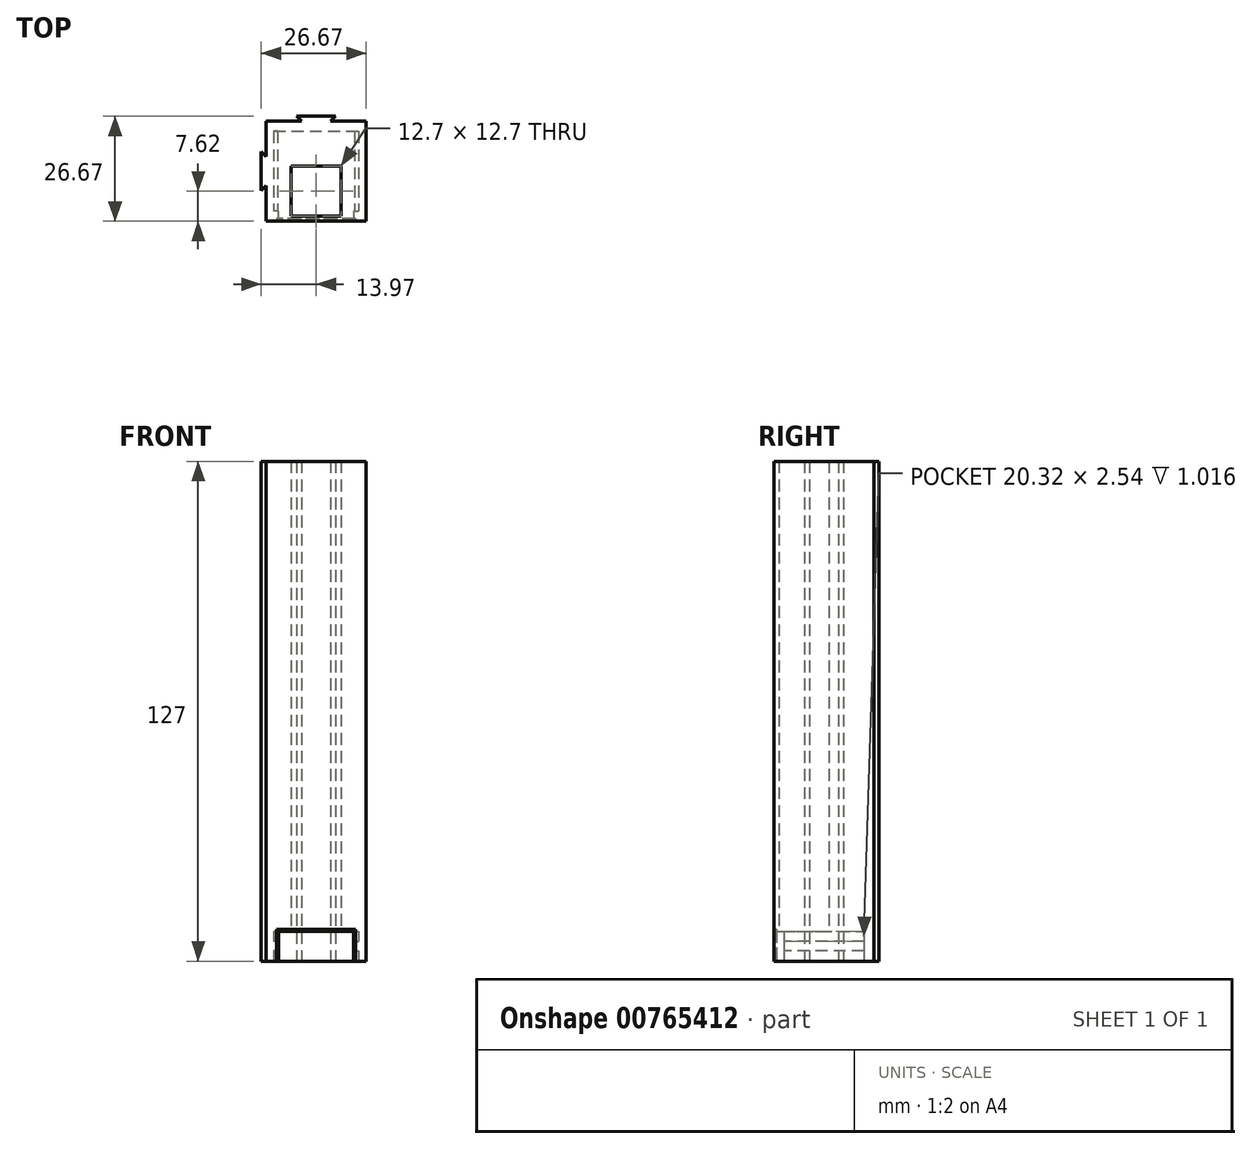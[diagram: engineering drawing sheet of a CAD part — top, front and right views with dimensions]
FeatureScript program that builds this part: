
annotation { "Feature Type Name" : "Feature", "Feature Type Description" : "" }
export const myFeature = defineFeature(function(context is Context, id is Id, definition is map)
    precondition{}
    {
        {
            var Q0;
            Q0=qCreatedBy(makeId("Top.planeOp"),FACE);
            var sketch = newSketch(context, id + "F0", { "sketchPlane" : qUnion([Q0])});
            skLineSegment(sketch, "E0.bottom", {"start": v(12.7, 12.7) * mm, "end": v(-12.7, 12.7) * mm});
            skLineSegment(sketch, "E0.top", {"start": v(12.7, -12.7) * mm, "end": v(-12.7, -12.7) * mm});
            skLineSegment(sketch, "E0.left", {"start": v(12.7, 12.7) * mm, "end": v(12.7, -12.7) * mm});
            skLineSegment(sketch, "E0.right", {"start": v(-12.7, 12.7) * mm, "end": v(-12.7, -12.7) * mm});
            skPoint(sketch, "E0.middle", {"position": v(0, 0) * mm});
            skLineSegment(sketch, "E1", {"start": v(-3.68, 12.7) * mm, "end": v(-4.95, 13.97) * mm});
            skLineSegment(sketch, "E2", {"start": v(-4.95, 13.97) * mm, "end": v(4.95, 13.97) * mm});
            skLineSegment(sketch, "E3", {"start": v(4.95, 13.97) * mm, "end": v(3.68, 12.7) * mm});
            skLineSegment(sketch, "E4.MirrorCS", {"start": v(-12.7, 3.68) * mm, "end": v(-13.97, 4.95) * mm});
            skLineSegment(sketch, "E5.MirrorCS", {"start": v(-13.97, 4.95) * mm, "end": v(-13.97, -4.95) * mm});
            skLineSegment(sketch, "E6.MirrorCS", {"start": v(-13.97, -4.95) * mm, "end": v(-12.7, -3.68) * mm});
            skLineSegment(sketch, "E7.bottom", {"start": v(-6.35, -11.43) * mm, "end": v(6.35, -11.43) * mm});
            skLineSegment(sketch, "E7.top", {"start": v(-6.35, 1.27) * mm, "end": v(6.35, 1.27) * mm});
            skLineSegment(sketch, "E7.left", {"start": v(-6.35, -11.43) * mm, "end": v(-6.35, 1.27) * mm});
            skLineSegment(sketch, "E7.right", {"start": v(6.35, -11.43) * mm, "end": v(6.35, 1.27) * mm});
            skPoint(sketch, "E7.middle", {"position": v(0, -5.08) * mm});
            skSolve(sketch);
        }
        {
            var Q0;
            Q0=makeQuery(id+"F0.imprint","IMPRINT",FACE,{"disambiguationData":[TD([[makeQuery(id+"F0.imprint","IMPRINT",EDGE,{"derivedFrom":sQuery(id+"F0.wireOp",EDGE,"Ek69CNRn-8RVK-RxQl-53fH-Jz5PkY7OIrkr")}),-1.0]])]});
            var Q1;
            {var subQ0=sQuery(id+"F0.wireOp",EDGE,"E4.MirrorCS");Q1=makeQuery(id+"F0.imprint","IMPRINT",FACE,{"disambiguationData":[TD([[makeQuery(id+"F0.imprint","IMPRINT",EDGE,{"derivedFrom":subQ0}),1.0]])]});}
            var Q2;
            {var subQ0=sQuery(id+"F0.wireOp",EDGE,"648ae852-5b30-4ce4-b5d7-663e1538fe900.MirrorCS");Q2=makeQuery(id+"F0.imprint","IMPRINT",FACE,{"disambiguationData":[TD([[makeQuery(id+"F0.imprint","IMPRINT",EDGE,{"derivedFrom":subQ0}),1.0]])]});}
            var Q3;
            {var subQ0=sQuery(id+"F0.wireOp",EDGE,"995b501b-87b1-40df-89db-5718103b703a");Q3=makeQuery(id+"F0.imprint","IMPRINT",FACE,{"disambiguationData":[TD([[makeQuery(id+"F0.imprint","IMPRINT",EDGE,{"derivedFrom":subQ0}),-1.0]])]});}
            var Q4;
            {var subQ0=sQuery(id+"F0.wireOp",EDGE,"E1");Q4=makeQuery(id+"F0.imprint","IMPRINT",FACE,{"disambiguationData":[TD([[makeQuery(id+"F0.imprint","IMPRINT",EDGE,{"derivedFrom":subQ0}),-1.0]])]});}
            var Q5;
            {var subQ1=sQuery(id+"F0.wireOp",EDGE,"E0.top");Q5=makeQuery(id+"F0.imprint","IMPRINT",FACE,{"disambiguationData":[TD([[makeQuery(id+"F0.imprint","IMPRINT",EDGE,{"derivedFrom":subQ1}),-1.0]])]});}
            extrude(context, id + "F1", {"entities" : qUnion([Q0, Q1, Q2, Q3, Q4, Q5]), "depth" : 127 * mm, "offsetDistance" : 25.4 * mm});
        }
        {
            var Q0;
            Q0=makeQuery(id+"F1.opExtrude","CAP_FACE",FACE,{"disambiguationData":[OSD([sQuery(id+"F0.wireOp",EDGE,"E0.bottom"),sQuery(id+"F0.wireOp",EDGE,"E0.top"),sQuery(id+"F0.wireOp",EDGE,"E0.left"),sQuery(id+"F0.wireOp",EDGE,"E0.right"),sQuery(id+"F0.wireOp",EDGE,"E1"),sQuery(id+"F0.wireOp",EDGE,"E2"),sQuery(id+"F0.wireOp",EDGE,"E3"),sQuery(id+"F0.wireOp",EDGE,"995b501b-87b1-40df-89db-5718103b703a"),sQuery(id+"F0.wireOp",EDGE,"d9b632a0-34b0-463a-8696-1e9d1799fc8a"),sQuery(id+"F0.wireOp",EDGE,"b3bc504c-1797-48d5-8887-40c9249a8113"),sQuery(id+"F0.wireOp",EDGE,"E4.MirrorCS"),sQuery(id+"F0.wireOp",EDGE,"E5.MirrorCS"),sQuery(id+"F0.wireOp",EDGE,"E6.MirrorCS"),sQuery(id+"F0.wireOp",EDGE,"Ek69CNRn-8RVK-RxQl-53fH-Jz5PkY7OIrkr")])],"isStart":true});
            var sketch = newSketch(context, id + "F2", { "sketchPlane" : qUnion([Q0])});
            skLineSegment(sketch, "E8", {"start": v(-9.52, 12.7) * mm, "end": v(-9.52, 10.16) * mm});
            skLineSegment(sketch, "E9", {"start": v(-9.52, 10.16) * mm, "end": v(-10.8, 10.16) * mm});
            skLineSegment(sketch, "E10", {"start": v(-10.8, 10.16) * mm, "end": v(-10.8, -10.16) * mm});
            skLineSegment(sketch, "E11", {"start": v(-10.8, -10.16) * mm, "end": v(10.8, -10.16) * mm});
            skLineSegment(sketch, "E12", {"start": v(10.8, -10.16) * mm, "end": v(10.8, 10.16) * mm});
            skLineSegment(sketch, "E13", {"start": v(9.52, 10.16) * mm, "end": v(10.8, 10.16) * mm});
            skLineSegment(sketch, "E14", {"start": v(9.52, 10.16) * mm, "end": v(9.52, 12.7) * mm});
            skLineSegment(sketch, "E15", {"start": v(9.52, 12.7) * mm, "end": v(-9.52, 12.7) * mm});
            skSolve(sketch);
        }
        {
            var Q0;
            Q0=makeQuery(id+"F2.imprint","IMPRINT",FACE,{"disambiguationData":[TD([[makeQuery(id+"F2.imprint","IMPRINT",EDGE,{"derivedFrom":sQuery(id+"F2.wireOp",EDGE,"E8")}),1.0]])]});
            extrude(context, id + "F3", {"entities" : qUnion([Q0]), "operationType" : NewBodyOperationType.REMOVE, "oppositeDirection" : true, "depth" : 7.62 * mm, "offsetDistance" : 25.4 * mm});
        }
        {
            var Q0;
            Q0=makeQuery(id+"F1.opExtrude","SWEPT_FACE",FACE,{"disambiguationData":[OSD([sQuery(id+"F0.wireOp",EDGE,"E0.top")])]});
            var sketch = newSketch(context, id + "F4", { "sketchPlane" : qUnion([Q0])});
            skLineSegment(sketch, "E16.0", {"start": v(-10.03, 8.13) * mm, "end": v(-10.03, 0) * mm});
            skLineSegment(sketch, "E16.1", {"start": v(10.03, 8.13) * mm, "end": v(-10.03, 8.13) * mm});
            skLineSegment(sketch, "E16.2", {"start": v(10.03, 8.13) * mm, "end": v(10.03, 0) * mm});
            skSolve(sketch);
        }
        {
            var Q0;
            {var subQ13=sQuery(id+"F4.wireOp",EDGE,"E16.0");Q0=makeQuery(id+"F4.imprint","IMPRINT",FACE,{"disambiguationData":[TD([[makeQuery(id+"F4.imprint","IMPRINT",EDGE,{"derivedFrom":subQ13}),1.0]])]});}
            extrude(context, id + "F5", {"entities" : qUnion([Q0]), "operationType" : NewBodyOperationType.REMOVE, "oppositeDirection" : true, "depth" : 0.64 * mm, "offsetDistance" : 25.4 * mm});
        }
        {
            var Q0;
            Q0=makeQuery(id+"F3.boolean.opBoolean","COPY",FACE,{"derivedFrom":makeQuery(id+"F3.opExtrude","SWEPT_FACE",FACE,{"disambiguationData":[OSD([sQuery(id+"F2.wireOp",EDGE,"E10")])]})});
            var sketch = newSketch(context, id + "F6", { "sketchPlane" : qUnion([Q0])});
            skLineSegment(sketch, "E17.bottom", {"start": v(10.16, 5.08) * mm, "end": v(-10.16, 5.08) * mm});
            skLineSegment(sketch, "E17.top", {"start": v(10.16, 2.67) * mm, "end": v(-10.16, 2.67) * mm});
            skLineSegment(sketch, "E17.left", {"start": v(10.16, 5.08) * mm, "end": v(10.16, 2.67) * mm});
            skLineSegment(sketch, "E17.right", {"start": v(-10.16, 5.08) * mm, "end": v(-10.16, 2.67) * mm});
            skSolve(sketch);
        }
        {
            var Q0;
            Q0=makeQuery(id+"F6.imprint","IMPRINT",FACE,{"disambiguationData":[TD([[makeQuery(id+"F6.imprint","IMPRINT",EDGE,{"derivedFrom":sQuery(id+"F6.wireOp",EDGE,"E17.bottom")}),1.0]])]});
            extrude(context, id + "F7", {"entities" : qUnion([Q0]), "depth" : 1.02 * mm, "offsetDistance" : 25.4 * mm});
        }
        {
            var Q0;
            Q0=makeQuery(id+"F7.opExtrude","SWEPT_BODY",BODY,{"disambiguationData":[OSD([sQuery(id+"F6.wireOp",EDGE,"E17.bottom"),sQuery(id+"F6.wireOp",EDGE,"E17.top"),sQuery(id+"F6.wireOp",EDGE,"E17.left"),sQuery(id+"F6.wireOp",EDGE,"E17.right")])]});
            var Q1;
            Q1=qCreatedBy(makeId("Right.planeOp"),FACE);
            mirror(context, id + "F8", {"operationType" : NewBodyOperationType.ADD, "entities" : qUnion([Q0]), "mirrorPlane" : qUnion([Q1])});
        }
        {
            var Q0;
            Q0=makeQuery(id+"F1.opExtrude","SWEPT_BODY",BODY,{"disambiguationData":[OSD([sQuery(id+"F0.wireOp",EDGE,"E0.bottom"),sQuery(id+"F0.wireOp",EDGE,"E0.top"),sQuery(id+"F0.wireOp",EDGE,"E0.left"),sQuery(id+"F0.wireOp",EDGE,"E0.right"),sQuery(id+"F0.wireOp",EDGE,"E1"),sQuery(id+"F0.wireOp",EDGE,"E2"),sQuery(id+"F0.wireOp",EDGE,"E3"),sQuery(id+"F0.wireOp",EDGE,"995b501b-87b1-40df-89db-5718103b703a"),sQuery(id+"F0.wireOp",EDGE,"d9b632a0-34b0-463a-8696-1e9d1799fc8a"),sQuery(id+"F0.wireOp",EDGE,"b3bc504c-1797-48d5-8887-40c9249a8113"),sQuery(id+"F0.wireOp",EDGE,"E4.MirrorCS"),sQuery(id+"F0.wireOp",EDGE,"E5.MirrorCS"),sQuery(id+"F0.wireOp",EDGE,"E6.MirrorCS"),sQuery(id+"F0.wireOp",EDGE,"Ek69CNRn-8RVK-RxQl-53fH-Jz5PkY7OIrkr")])]});
            transform(context, id + "F9", {"entities" : qUnion([Q0]), "transformType" : TransformType.TRANSLATION_3D, "dx" : 0 * mm, "dy" : 0 * mm, "dz" : 0 * mm, "makeCopy" : true});
        }
        {
            var Q0;
            Q0=makeQuery(id+"F9.opPattern","COPY",BODY,{"derivedFrom":makeQuery(id+"F1.opExtrude","SWEPT_BODY",BODY,{"disambiguationData":[OSD([sQuery(id+"F0.wireOp",EDGE,"E0.bottom"),sQuery(id+"F0.wireOp",EDGE,"E0.top"),sQuery(id+"F0.wireOp",EDGE,"E0.left"),sQuery(id+"F0.wireOp",EDGE,"E0.right"),sQuery(id+"F0.wireOp",EDGE,"E1"),sQuery(id+"F0.wireOp",EDGE,"E2"),sQuery(id+"F0.wireOp",EDGE,"E3"),sQuery(id+"F0.wireOp",EDGE,"995b501b-87b1-40df-89db-5718103b703a"),sQuery(id+"F0.wireOp",EDGE,"d9b632a0-34b0-463a-8696-1e9d1799fc8a"),sQuery(id+"F0.wireOp",EDGE,"b3bc504c-1797-48d5-8887-40c9249a8113"),sQuery(id+"F0.wireOp",EDGE,"E4.MirrorCS"),sQuery(id+"F0.wireOp",EDGE,"E5.MirrorCS"),sQuery(id+"F0.wireOp",EDGE,"E6.MirrorCS"),sQuery(id+"F0.wireOp",EDGE,"E7.bottom"),sQuery(id+"F0.wireOp",EDGE,"E7.top"),sQuery(id+"F0.wireOp",EDGE,"E7.left"),sQuery(id+"F0.wireOp",EDGE,"E7.right")])]}),"instanceName":"1"});
            deleteBodies(context, id + "F10", {"entities" : qUnion([Q0])});
        }
    });
